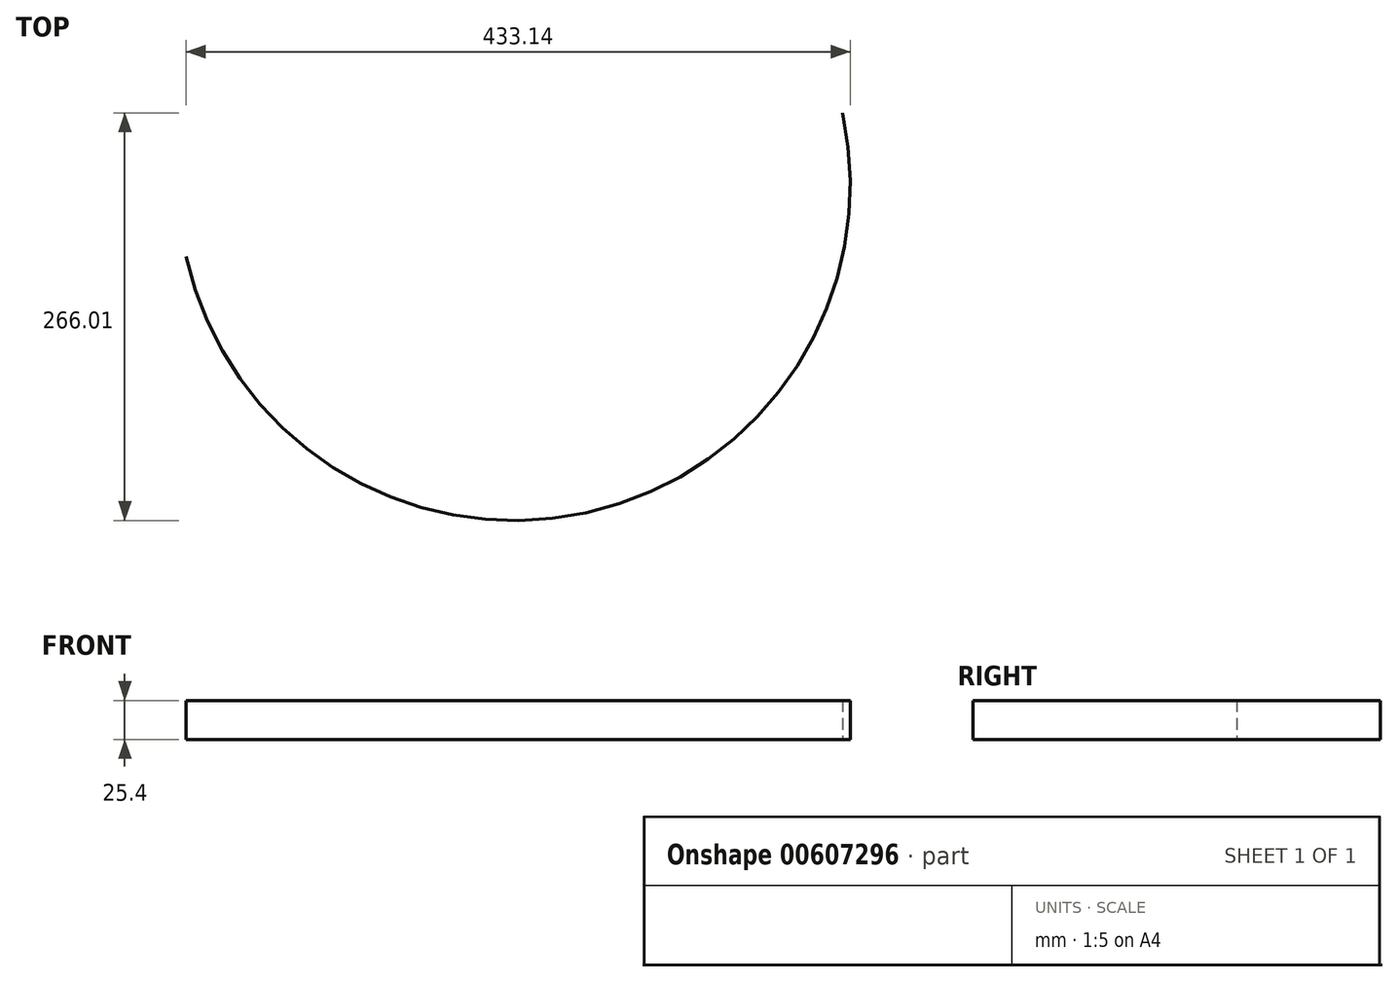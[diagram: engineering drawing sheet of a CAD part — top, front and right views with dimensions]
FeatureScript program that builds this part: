
annotation { "Feature Type Name" : "Feature", "Feature Type Description" : "" }
export const myFeature = defineFeature(function(context is Context, id is Id, definition is map)
    precondition{}
    {
        {
            var Q0;
            Q0=qCreatedBy(makeId("Top.planeOp"),FACE);
            var sketch = newSketch(context, id + "F0", { "sketchPlane" : qUnion([Q0])});
            skArc(sketch, "E0", {"start": v(-193.85, 60.91) * mm, "mid": v(67.09, -106.21) * mm, "end": v(234.21, 154.72) * mm});
            skSolve(sketch);
        }
        {
            var Q0;
            Q0=sQuery(id+"F0.wireOp",EDGE,"E0");
            extrude(context, id + "F1", {"bodyType" : ToolBodyType.SURFACE, "surfaceEntities" : qUnion([Q0]), "endBound" : BoundingType.SYMMETRIC, "oppositeDirection" : true, "depth" : 25.4 * mm, "offsetDistance" : 25.4 * mm});
        }
    });
